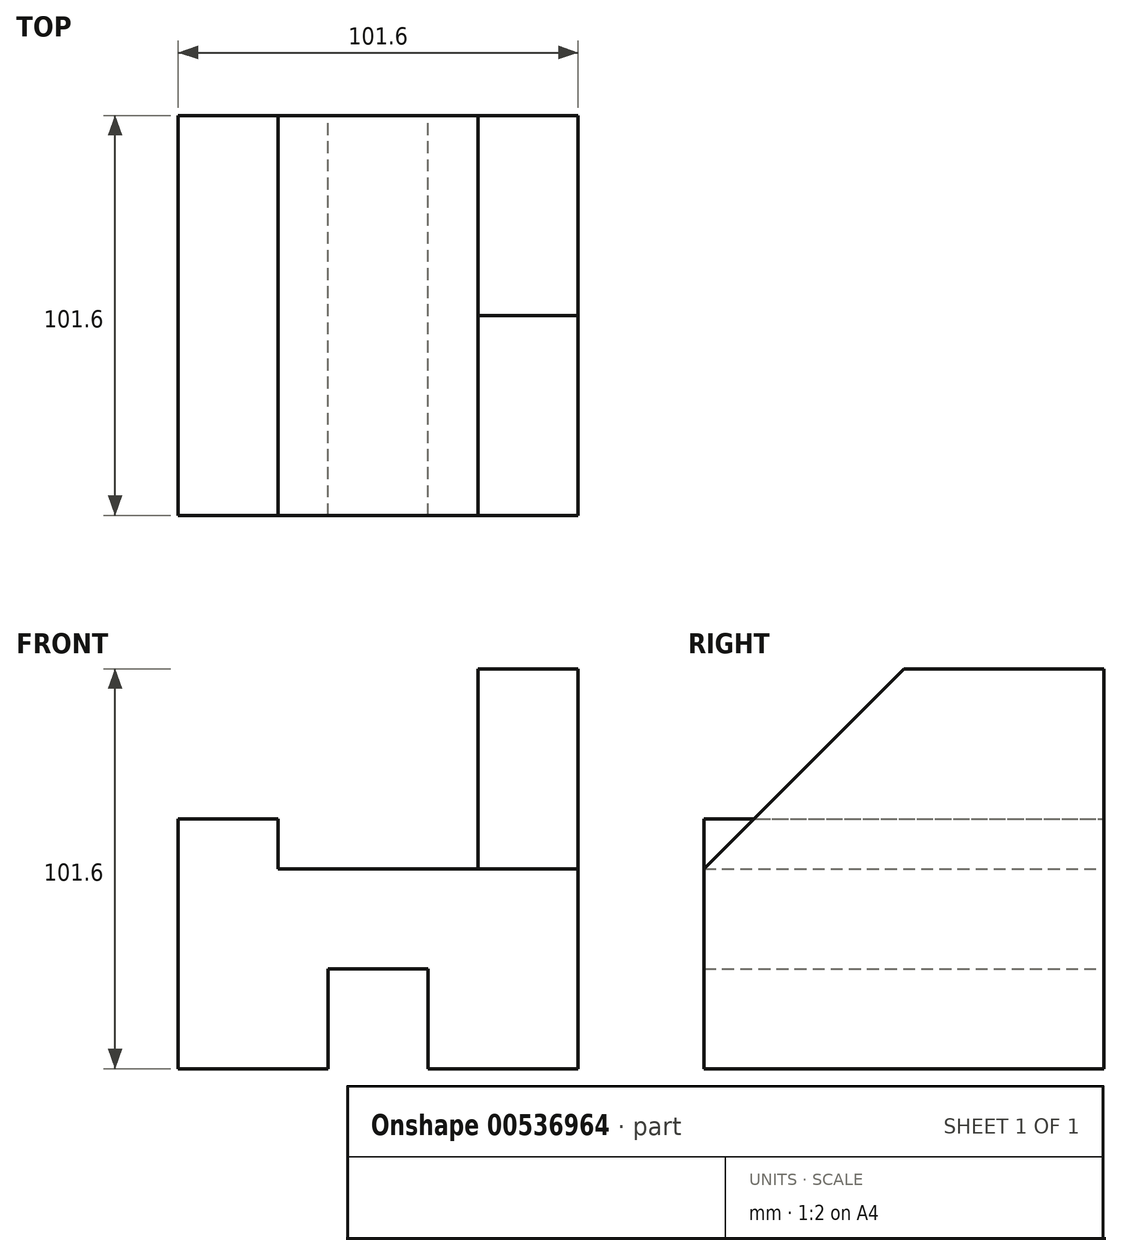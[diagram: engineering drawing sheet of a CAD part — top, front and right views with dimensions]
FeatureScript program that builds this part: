
annotation { "Feature Type Name" : "Feature", "Feature Type Description" : "" }
export const myFeature = defineFeature(function(context is Context, id is Id, definition is map)
    precondition{}
    {
        {
            var Q0;
            Q0=qCreatedBy(makeId("Front.planeOp"),FACE);
            var sketch = newSketch(context, id + "F0", { "sketchPlane" : qUnion([Q0])});
            skLineSegment(sketch, "E0", {"start": v(0, 0) * mm, "end": v(-38.1, 0) * mm});
            skLineSegment(sketch, "E1", {"start": v(-38.1, 0) * mm, "end": v(-38.1, 25.4) * mm});
            skLineSegment(sketch, "E2", {"start": v(-38.1, 25.4) * mm, "end": v(-63.5, 25.4) * mm});
            skLineSegment(sketch, "E3", {"start": v(-63.5, 25.4) * mm, "end": v(-63.5, 0) * mm});
            skLineSegment(sketch, "E4", {"start": v(-63.5, 0) * mm, "end": v(-101.6, 0) * mm});
            skLineSegment(sketch, "E5", {"start": v(-101.6, 0) * mm, "end": v(-101.6, 63.5) * mm});
            skLineSegment(sketch, "E6", {"start": v(-101.6, 63.5) * mm, "end": v(-76.2, 63.5) * mm});
            skLineSegment(sketch, "E7", {"start": v(-76.2, 63.5) * mm, "end": v(-76.2, 50.8) * mm});
            skLineSegment(sketch, "E8", {"start": v(-76.2, 50.8) * mm, "end": v(-25.4, 50.8) * mm});
            skLineSegment(sketch, "E9", {"start": v(-25.4, 50.8) * mm, "end": v(-25.4, 101.6) * mm});
            skLineSegment(sketch, "E10", {"start": v(-25.4, 101.6) * mm, "end": v(0, 101.6) * mm});
            skLineSegment(sketch, "E11", {"start": v(0, 101.6) * mm, "end": v(0, 0) * mm});
            skSolve(sketch);
        }
        {
            var Q0;
            Q0 = qSketchRegion(id + "F0", true);
            extrude(context, id + "F1", {"entities" : qUnion([Q0]), "depth" : 101.6 * mm, "offsetDistance" : 25.4 * mm});
        }
        {
            var Q0;
            Q0=makeQuery(id+"F1.opExtrude","SWEPT_FACE",FACE,{"disambiguationData":[OSD([sQuery(id+"F0.wireOp",EDGE,"E11")])]});
            var sketch = newSketch(context, id + "F2", { "sketchPlane" : qUnion([Q0])});
            skLineSegment(sketch, "E12", {"start": v(-101.6, 0) * mm, "end": v(-101.6, 50.8) * mm});
            skLineSegment(sketch, "E13", {"start": v(0, 101.6) * mm, "end": v(-50.8, 101.6) * mm});
            skLineSegment(sketch, "E14", {"start": v(-50.8, 101.6) * mm, "end": v(-101.6, 50.8) * mm});
            skSolve(sketch);
        }
        {
            var Q0;
            Q0 = qSketchRegion(id + "F2", true);
            var Q1;
            {var subQ0=sQuery(id+"F2.wireOp",EDGE,"E14");Q1=makeQuery(id+"F2.imprint","IMPRINT",FACE,{"disambiguationData":[TD([[makeQuery(id+"F2.imprint","IMPRINT",EDGE,{"derivedFrom":subQ0}),-1.0]])]});}
            extrude(context, id + "F3", {"entities" : qUnion([Q0, Q1]), "operationType" : NewBodyOperationType.REMOVE, "oppositeDirection" : true, "depth" : 25.4 * mm, "offsetDistance" : 25.4 * mm});
        }
    });
